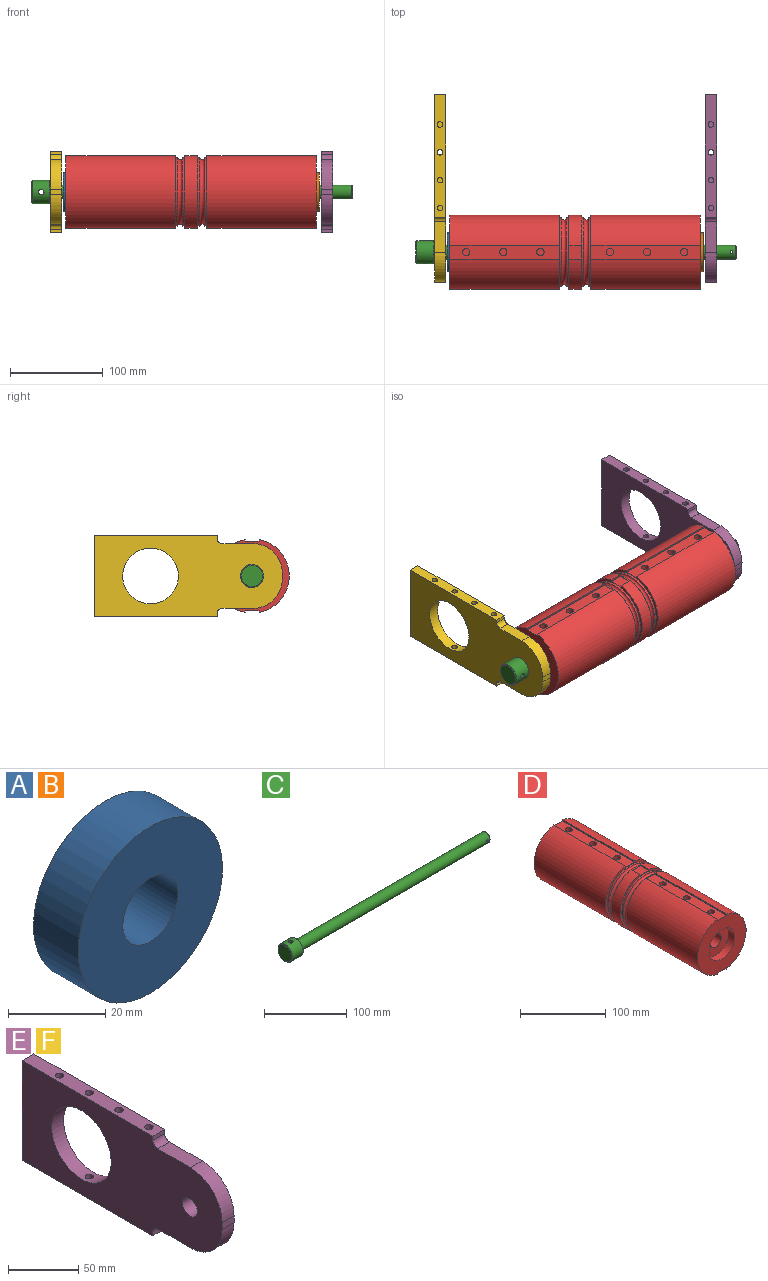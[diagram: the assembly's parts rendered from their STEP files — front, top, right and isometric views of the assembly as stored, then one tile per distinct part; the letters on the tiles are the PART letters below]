
ASSEMBLY  parts=6 mates=8
PART A: 4 faces, bbox 42x13x42 mm
  f0: cylinder r=8mm len=16mm, axis (0,1,0), area 653.5mm2, adj f2,f3
  f1: cylinder r=21mm len=42mm, axis (0,1,0), area 1715.3mm2, adj f2,f3
  f2: plane 42x42mm, normal (0,-1,0), area 1184.4mm2, adj f0,f1
  f3: plane 42x42mm, normal (0,1,0), area 1184.4mm2, adj f0,f1
PART B: same geometry as A
PART C: 10 faces, bbox 345x25x25 mm
  f0: plane 23x23mm, normal (-1,0,0), area 415.5mm2, adj f6
  f1: cylinder r=12.5mm len=25mm, axis (-1,0,0), area 1356.9mm2, adj f6,f7,f8
  f2: plane 23x23mm, normal (1,0,0), area 238.8mm2, adj f3,f7
  f3: cylinder r=7.5mm len=324mm, axis (-1,0,0), area 15254mm2, adj f2,f5,f9
  f4: plane 13x13mm, normal (1,0,0), area 132.7mm2, adj f5
  f5: cone r=7.5mm half-angle=45deg, axis (-1,0,0), area 62.2mm2, adj f3,f4
  f6: cone r=11.5mm half-angle=45deg, axis (1,0,0), area 106.6mm2, adj f0,f1
  f7: cone r=12.5mm half-angle=45deg, axis (-1,0,0), area 106.6mm2, adj f1,f2
  f8: cylinder r=3mm len=25mm, axis (0,0,1), area 464.4mm2, adj f1
  f9: cylinder r=1.5mm len=15mm, axis (0,1,0), area 139.9mm2, adj f3
PART D: 65 faces, bbox 83.9x270x83.9 mm
  f0: cylinder r=40mm len=118mm, axis (0,1,0), area 13047.8mm2, adj f2,f5,f12,f24
  f1: cylinder r=40mm len=118mm, axis (0,1,0), area 13047.8mm2, adj f3,f6,f12,f24
  f2: plane 118x1.79mm, normal (1,0,0), area 211.3mm2, adj f0,f4,f12,f24
  f3: plane 118x1.79mm, normal (-1,0,0), area 211.3mm2, adj f1,f4,f12,f24
  f4: plane 118x15mm, normal (0,0,-1), area 1619.2mm2, adj f2,f3,f12,f24,f59,f61,f63
  f5: plane 118x1.79mm, normal (1,0,0), area 211.3mm2, adj f0,f7,f12,f24
  f6: plane 118x1.79mm, normal (-1,0,0), area 211.3mm2, adj f1,f7,f12,f24
  f7: plane 118x15mm, normal (0,0,1), area 1619.2mm2, adj f5,f6,f12,f24,f47,f49,f51
  f8: cylinder r=9mm len=250mm, axis (0,1,0), area 14137.2mm2, adj f20,f22
  f9: cylinder r=40mm len=118mm, axis (0,1,0), area 13047.8mm2, adj f11,f13,f16,f36
  f10: cylinder r=40mm len=118mm, axis (0,1,0), area 13047.8mm2, adj f11,f14,f17,f36
  f11: plane 80x78.58mm, normal (0,1,0), area 3573.2mm2, adj f9,f10,f13,f14,f15,f16,f17,f18
  f12: plane 80x78.58mm, normal (0,-1,0), area 3573.2mm2, adj f0,f1,f2,f3,f4,f5,f6,f7
  f13: plane 118x1.79mm, normal (1,0,0), area 211.3mm2, adj f9,f11,f15,f36
  f14: plane 118x1.79mm, normal (-1,0,0), area 211.3mm2, adj f10,f11,f15,f36
  f15: plane 118x15mm, normal (0,0,-1), area 1619.2mm2, adj f11,f13,f14,f36,f53,f55,f57
  f16: plane 118x1.79mm, normal (1,0,0), area 211.3mm2, adj f9,f11,f18,f36
  f17: plane 118x1.79mm, normal (-1,0,0), area 211.3mm2, adj f10,f11,f18,f36
  f18: plane 118x15mm, normal (0,0,1), area 1619.2mm2, adj f11,f16,f17,f36,f41,f43,f45
  f19: cylinder r=21mm len=42mm, axis (0,-1,0), area 1319.5mm2, adj f12,f20
  f20: plane 42x42mm, normal (0,-1,0), area 1131mm2, adj f8,f19
  f21: cylinder r=21mm len=42mm, axis (0,1,0), area 1319.5mm2, adj f11,f22
  f22: plane 42x42mm, normal (0,1,0), area 1131mm2, adj f8,f21
  f23: plane 80x78.58mm, normal (0,-1,0), area 657.8mm2, adj f25,f28,f29,f30,f31,f32,f33,f34
  f24: plane 80x78.58mm, normal (0,1,0), area 657.8mm2, adj f0,f1,f2,f3,f4,f5,f6,f7
  f25: cylinder r=37mm len=74mm, axis (0,1,0), area 581.2mm2, adj f23,f27
  f26: cylinder r=37mm len=74mm, axis (0,1,0), area 581.2mm2, adj f24,f27
  f27: torus R=37mm, axis (0,1,0), area 1747.3mm2, adj f25,f26
  f28: plane 15x14mm, normal (0,0,-1), area 210mm2, adj f23,f29,f30,f37
  f29: plane 14x1.79mm, normal (-1,0,0), area 25.1mm2, adj f23,f28,f34,f37
  f30: plane 14x1.79mm, normal (1,0,0), area 25.1mm2, adj f23,f28,f35,f37
  f31: plane 15x14mm, normal (0,0,1), area 210mm2, adj f23,f32,f33,f37
  f32: plane 14x1.79mm, normal (-1,0,0), area 25.1mm2, adj f23,f31,f34,f37
  f33: plane 14x1.79mm, normal (1,0,0), area 25.1mm2, adj f23,f31,f35,f37
  f34: cylinder r=40mm len=78.58mm, axis (0,1,0), area 1548mm2, adj f23,f29,f32,f37
  f35: cylinder r=40mm len=78.58mm, axis (0,1,0), area 1548mm2, adj f23,f30,f33,f37
  f36: plane 80x78.58mm, normal (0,-1,0), area 657.8mm2, adj f9,f10,f13,f14,f15,f16,f17,f18
  f37: plane 80x78.58mm, normal (0,1,0), area 657.8mm2, adj f28,f29,f30,f31,f32,f33,f34,f35
  f38: cylinder r=37mm len=74mm, axis (0,1,0), area 581.2mm2, adj f36,f40
  f39: cylinder r=37mm len=74mm, axis (0,1,0), area 581.2mm2, adj f37,f40
  f40: torus R=37mm, axis (0,1,0), area 1747.3mm2, adj f38,f39
  f41: cylinder r=4mm len=10mm, axis (0,0,1), area 251.3mm2, adj f18,f42
  f42: plane 8x8mm, normal (0,0,1), area 50.3mm2, adj f41
  f43: cylinder r=4mm len=10mm, axis (0,0,1), area 251.3mm2, adj f18,f44
  f44: plane 8x8mm, normal (0,0,1), area 50.3mm2, adj f43
  f45: cylinder r=4mm len=10mm, axis (0,0,1), area 251.3mm2, adj f18,f46
  f46: plane 8x8mm, normal (0,0,1), area 50.3mm2, adj f45
  f47: cylinder r=4mm len=10mm, axis (0,0,1), area 251.3mm2, adj f7,f48
  f48: plane 8x8mm, normal (0,0,1), area 50.3mm2, adj f47
  f49: cylinder r=4mm len=10mm, axis (0,0,1), area 251.3mm2, adj f7,f50
  f50: plane 8x8mm, normal (0,0,1), area 50.3mm2, adj f49
  f51: cylinder r=4mm len=10mm, axis (0,0,1), area 251.3mm2, adj f7,f52
  f52: plane 8x8mm, normal (0,0,1), area 50.3mm2, adj f51
  f53: cylinder r=4mm len=10mm, axis (0,0,-1), area 251.3mm2, adj f15,f54
  f54: plane 8x8mm, normal (0,0,-1), area 50.3mm2, adj f53
  f55: cylinder r=4mm len=10mm, axis (0,0,-1), area 251.3mm2, adj f15,f56
  f56: plane 8x8mm, normal (0,0,-1), area 50.3mm2, adj f55
  f57: cylinder r=4mm len=10mm, axis (0,0,-1), area 251.3mm2, adj f15,f58
  f58: plane 8x8mm, normal (0,0,-1), area 50.3mm2, adj f57
  f59: cylinder r=4mm len=10mm, axis (0,0,-1), area 251.3mm2, adj f4,f60
  f60: plane 8x8mm, normal (0,0,-1), area 50.3mm2, adj f59
  f61: cylinder r=4mm len=10mm, axis (0,0,-1), area 251.3mm2, adj f4,f62
  f62: plane 8x8mm, normal (0,0,-1), area 50.3mm2, adj f61
  f63: cylinder r=4mm len=10mm, axis (0,0,-1), area 251.3mm2, adj f4,f64
  f64: plane 8x8mm, normal (0,0,-1), area 50.3mm2, adj f63
PART E: 30 faces, bbox 12x202x87 mm
  f0: cylinder r=30mm len=60mm, axis (-1,0,0), area 2205.3mm2, adj f14,f15,f16,f23
  f1: cylinder r=5mm len=12mm, axis (-1,0,0), area 94.2mm2, adj f2,f13,f14,f15
  f2: plane 33x12mm, normal (0,0,1), area 396mm2, adj f1,f3,f14,f15
  f3: cylinder r=32mm len=32mm, axis (-1,0,0), area 603.2mm2, adj f2,f4,f14,f15
  f4: plane 12x6mm, normal (0,-1,0), area 72mm2, adj f3,f5,f14,f15
  f5: cylinder r=32mm len=32mm, axis (-1,0,0), area 603.2mm2, adj f4,f6,f14,f15
  f6: plane 33x12mm, normal (0,0,-1), area 396mm2, adj f5,f7,f14,f15
  f7: cylinder r=5mm len=12mm, axis (-1,0,0), area 94.2mm2, adj f6,f8,f14,f15
  f8: plane 12x3.5mm, normal (0,-1,0), area 42mm2, adj f7,f9,f14,f15
  f9: plane 132x12mm, normal (0,0,-1), area 1470.9mm2, adj f8,f10,f14,f15,f23,f24,f26,f28
  f10: plane 87x12mm, normal (0,1,0), area 1044mm2, adj f9,f11,f14,f15
  f11: plane 132x12mm, normal (0,0,1), area 1470.9mm2, adj f10,f13,f14,f15,f16,f17,f19,f21
  f12: cylinder r=7.5mm len=15mm, axis (-1,0,0), area 565.5mm2, adj f14,f15
  f13: plane 12x3.5mm, normal (0,-1,0), area 42mm2, adj f1,f11,f14,f15
  f14: plane 202x87mm, normal (1,0,0), area 12951.1mm2, adj f0,f1,f2,f3,f4,f5,f6,f7
  f15: plane 202x87mm, normal (-1,0,0), area 12951.1mm2, adj f0,f1,f2,f3,f4,f5,f6,f7
  f16: cylinder r=3mm len=13.92mm, axis (0,0,1), area 257.2mm2, adj f0,f11
  f17: cylinder r=3mm len=20mm, axis (0,0,1), area 377mm2, adj f11,f18
  f18: plane 6x6mm, normal (0,0,1), area 28.3mm2, adj f17
  f19: cylinder r=3mm len=20mm, axis (0,0,1), area 377mm2, adj f11,f20
  f20: plane 6x6mm, normal (0,0,1), area 28.3mm2, adj f19
  f21: cylinder r=3mm len=20mm, axis (0,0,1), area 377mm2, adj f11,f22
  f22: plane 6x6mm, normal (0,0,1), area 28.3mm2, adj f21
  f23: cylinder r=3mm len=13.92mm, axis (0,0,-1), area 257.1mm2, adj f0,f9
  f24: cylinder r=3mm len=20mm, axis (0,0,-1), area 377mm2, adj f9,f25
  f25: plane 6x6mm, normal (0,0,-1), area 28.3mm2, adj f24
  f26: cylinder r=3mm len=20mm, axis (0,0,-1), area 377mm2, adj f9,f27
  f27: plane 6x6mm, normal (0,0,-1), area 28.3mm2, adj f26
  f28: cylinder r=3mm len=20mm, axis (0,0,-1), area 377mm2, adj f9,f29
  f29: plane 6x6mm, normal (0,0,-1), area 28.3mm2, adj f28
PART F: same geometry as E
PLACE A rot(axis=(0.58,-0.58,0.58),120deg) t=(-66.83,455.68,-17.59)mm
PLACE B rot(axis=(0.71,0.71,0),180deg) t=(209.17,455.68,-17.59)mm
PLACE C rot(axis=(1,0,0),90deg) t=(-100.42,455.68,-17.59)mm
PLACE D rot(axis=(0,0,1),90deg) t=(-63.83,455.68,-17.59)mm
PLACE E t=(211.62,423.18,-52.59)mm
PLACE F t=(-80.42,423.18,-52.59)mm
MATE cylindrical C.f1 <-> E.f12  axis (-1,0,0) through (81.58,455.68,-17.59)mm
MATE planar B.f1 <-> D.f19  axis (-1,0,0) through (196.17,455.68,-17.59)mm
MATE cylindrical A.f1 <-> D.f19  axis (-1,0,0) through (-53.83,455.68,-17.59)mm
MATE planar F.f15 <-> C.f1  axis (-1,0,0) through (-80.42,525.39,-17.59)mm
MATE cylindrical C.f1 <-> F.f12  axis (-1,0,0) through (-80.42,455.68,-17.59)mm
MATE cylindrical B.f1 <-> D.f19  axis (1,0,0) through (196.17,455.68,-17.59)mm
MATE planar D.f19 <-> A.f1  axis (-1,0,0) through (-53.83,455.68,-17.59)mm
MATE cylindrical A.f0 <-> C.f1  axis (-1,0,0) through (-66.83,455.68,-17.59)mm
